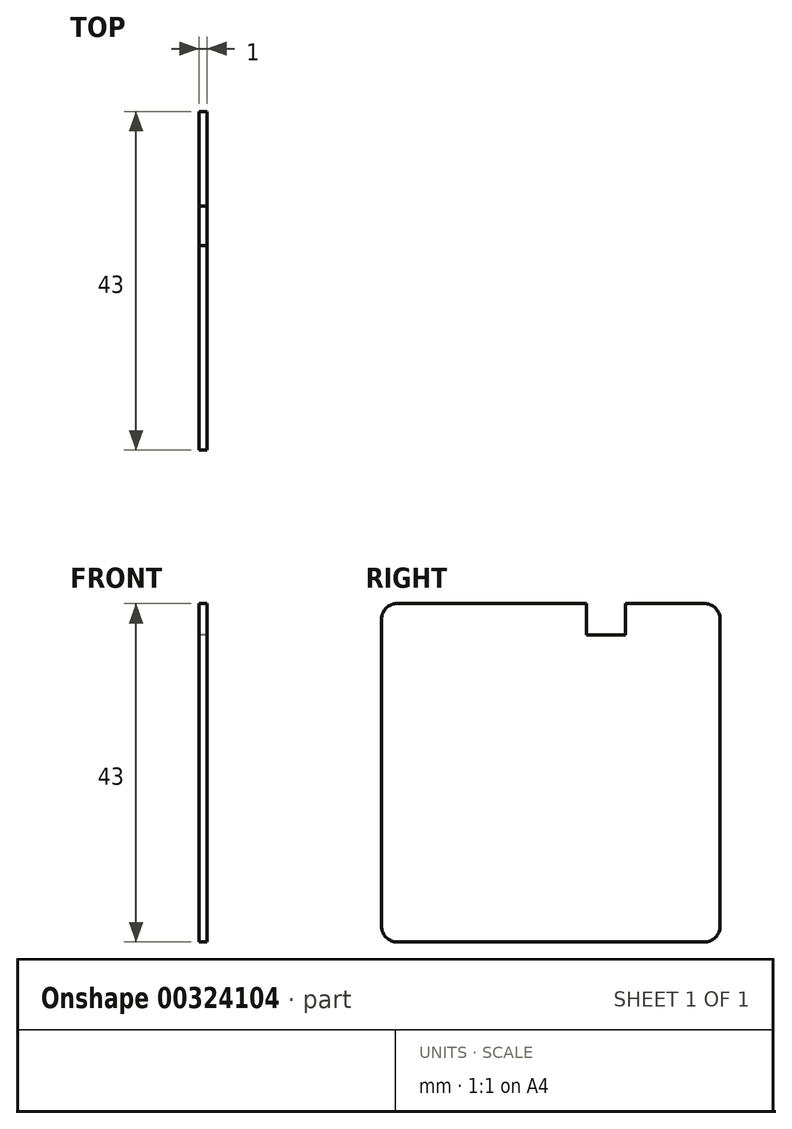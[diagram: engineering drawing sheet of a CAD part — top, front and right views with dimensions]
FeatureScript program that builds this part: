
annotation { "Feature Type Name" : "Feature", "Feature Type Description" : "" }
export const myFeature = defineFeature(function(context is Context, id is Id, definition is map)
    precondition{}
    {
        {
            var Q0;
            Q0=qCreatedBy(makeId("Right.planeOp"),FACE);
            var sketch = newSketch(context, id + "F0", { "sketchPlane" : qUnion([Q0])});
            skLineSegment(sketch, "E0.top", {"start": v(-15.4, -16.33) * mm, "end": v(27.6, -16.33) * mm});
            skLineSegment(sketch, "E0.left", {"start": v(-15.4, 26.67) * mm, "end": v(-15.4, -16.33) * mm});
            skLineSegment(sketch, "E0.right", {"start": v(27.6, 26.67) * mm, "end": v(27.6, -16.33) * mm});
            skLineSegment(sketch, "E1.top", {"start": v(10.6, 22.67) * mm, "end": v(15.6, 22.67) * mm});
            skLineSegment(sketch, "E1.left", {"start": v(10.6, 26.67) * mm, "end": v(10.6, 22.67) * mm});
            skLineSegment(sketch, "E1.right", {"start": v(15.6, 26.67) * mm, "end": v(15.6, 22.67) * mm});
            skLineSegment(sketch, "E2", {"start": v(-15.4, 26.67) * mm, "end": v(10.6, 26.67) * mm});
            skLineSegment(sketch, "E3", {"start": v(15.6, 26.67) * mm, "end": v(27.6, 26.67) * mm});
            skSolve(sketch);
        }
        {
            var Q0;
            Q0 = qSketchRegion(id + "F0", true);
            extrude(context, id + "F1", {"entities" : qUnion([Q0]), "depth" : 1 * mm});
        }
        {
            var Q0;
            Q0=makeQuery(id+"F1.opExtrude","SWEPT_EDGE",EDGE,{"disambiguationData":[OSD([sQuery(id+"F0.wireOp",EDGE,"E0.bottom"),sQuery(id+"F0.wireOp",EDGE,"E0.left")])]});
            var Q1;
            Q1=makeQuery(id+"F1.opExtrude","SWEPT_EDGE",EDGE,{"disambiguationData":[OSD([sQuery(id+"F0.wireOp",EDGE,"E0.bottom"),sQuery(id+"F0.wireOp",EDGE,"E0.right")])]});
            fillet(context, id + "F2", {"entities" : qUnion([Q0, Q1]), "radius" : 2 * mm, "tangentPropagation" : true, "allowEdgeOverflow" : false});
        }
    });
